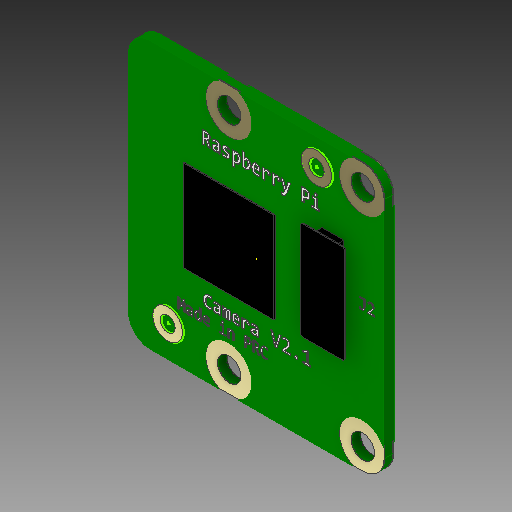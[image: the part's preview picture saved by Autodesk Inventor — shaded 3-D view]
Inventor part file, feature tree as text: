
AUTODESK INVENTOR PART (.ipt)
format: ipt  version: 2019 (Build 230136000, 136)  size: 2,345,472 bytes
history: native  units: mm
features: other x18, extrude x10, sketch x5, projected_geometry x5, hole x1, fillet x1
ambient origin geometry x8: Origin, YZ Plane, XZ Plane, XY Plane, X Axis, Y Axis, Z Axis, Center Point
bodies: Body1 (feature_tree), Body2 (feature_tree), Body3 (feature_tree), Body4 (feature_tree), Body5 (feature_tree), Body6 (feature_tree), Body7 (feature_tree), Body8 (feature_tree), Body9 (feature_tree)
feature tree (40):
  other  "PCB"
  sketch  "Boceto1"  dims[d0=23.862mm d1=25.0mm]
  extrude  "PCB_EXT"  Depth=25.0mm
  hole  "PADS_PCB_DRILL"  [1 undecoded]
  sketch  "Boceto2"  dims[d7=2.0mm d8=2.0mm]
  extrude  "PADS_PCB_DRILL_EXT"  Depth=1.0mm TaperAngle=0.0deg
  other  "FOTO"
  other  "SUPERIOR_PADS"
  extrude  "PADS_GOLDEN_UPPER_EXT"  Depth=2.2mm
  other  "INFERIOR_PADS"
  extrude  "PADS_GOLDEN_LOWER_EXT"  Depth=0.2mm
  extrude  "TEXTS_EXT"  Depth=0.2mm
  other  "REF_CON"
  extrude  "CONN"  Depth=0.2mm
  extrude  "CAM_BED"  Depth=0.2mm TaperAngle=0.0deg
  other  "PLANO_CON"
  extrude  "CONN_TOP"  Depth=0.2mm
  fillet  "Empalme2"  [1 undecoded]
  other  "REF_PADS_DRAW"
  extrude  "REF_PADS_DIAGONAL"  Depth=0.2mm TaperAngle=0.0deg
  extrude  "REF_PAD_BACK"  TaperAngle=90.0deg  [1 undecoded]
  other  "Imagen3"
  sketch  "Boceto4"  dims[d9=20.0mm d11=12.5mm d12=20.0mm d14=21.0mm d17=1.0mm d18=0.0mm]
  projected_geometry  "Contorno proyectado1"
  other  "PADS_UPPER"
  sketch  "Boceto5"  dims[d19=2.2mm d20=6.0mm d21=4.4mm d22=0.12mm d23=90.0deg d24=8.0mm d25=20.594885mm d26=2.0mm]
  projected_geometry  "Contorno proyectado2"
  projected_geometry  "Contorno proyectado3"
  projected_geometry  "Contorno proyectado4"
  projected_geometry  "Contorno proyectado5"
  other  "PADS_LOWER"
  other  "text_front"
  other  "TEXTS"
  other  "CAMERA_BED"
  sketch  "Boceto8"  dims[d27=4.4mm d28=4.4mm d29=4.4mm d30=4.4mm d31=0.13mm d32=0.0mm d57=24.8mm d63=90.0deg d66=0.07mm d67=0.0mm d68=90.0deg d69=0.07mm d70=0.0mm d71=0.03mm d72=0.0mm d74=8.5mm d75=8.5mm d78=5.212mm d79=8.25mm d82=4.7mm d86=2.2mm d87=8.5mm d88=0.5mm d89=1.0mm d90=0.0mm d91=0.1mm d92=0.0mm d93=90.0deg d94=0.1mm d95=0.0mm d97=0.2mm d98=13.8mm d101=0.1mm d102=0.0mm d115=0.1mm d116=0.0mm]
  other  "CONNECTOR"
  other  "PLACEMENT_CAM"
  other  "OUTSIDE_REF"
  other  "ref_pad_back_draw"
  other  "REF_PAD_BACK_PCB"
note: 3 required parameter values undecoded (feature->parameter linkage not recoverable at this tier; creation-order binding heuristic only, values carry confidence <= 0.55)
